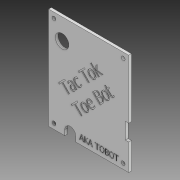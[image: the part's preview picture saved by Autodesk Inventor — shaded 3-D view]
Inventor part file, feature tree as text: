
AUTODESK INVENTOR PART (.ipt)
format: ipt  version: 2020 (Build 240168000, 168)  size: 538,112 bytes
history: native  units: mm
features: extrude x3, sketch x3
ambient origin geometry x8: Origin, YZ Plane, XZ Plane, XY Plane, X Axis, Y Axis, Z Axis, Center Point
bodies: Solid1 (feature_tree)
feature tree (6):
  extrude  "Extrusion1"  Depth=94.0mm
  extrude  "Extrusion2"  Depth=64.0mm
  extrude  "Extrusion3"  Depth=2.5mm TaperAngle=0.0deg
  sketch  "Sketch1"  dims[d0=74.0mm d1=94.0mm]
  sketch  "Sketch2"  dims[d2=84.0mm d3=64.0mm]
  sketch  "Sketch3"  dims[d4=3.5mm d5=2.5mm d6=0.0mm d7=27.0mm d8=15.0mm d9=3.0mm d10=19.5mm d11=12.5mm d12=12.5mm d13=5.0mm d14=5.0mm d15=15.0mm d16=0.0mm d17=0.0mm d20=45.0deg d21=0.5mm d22=0.0mm]
